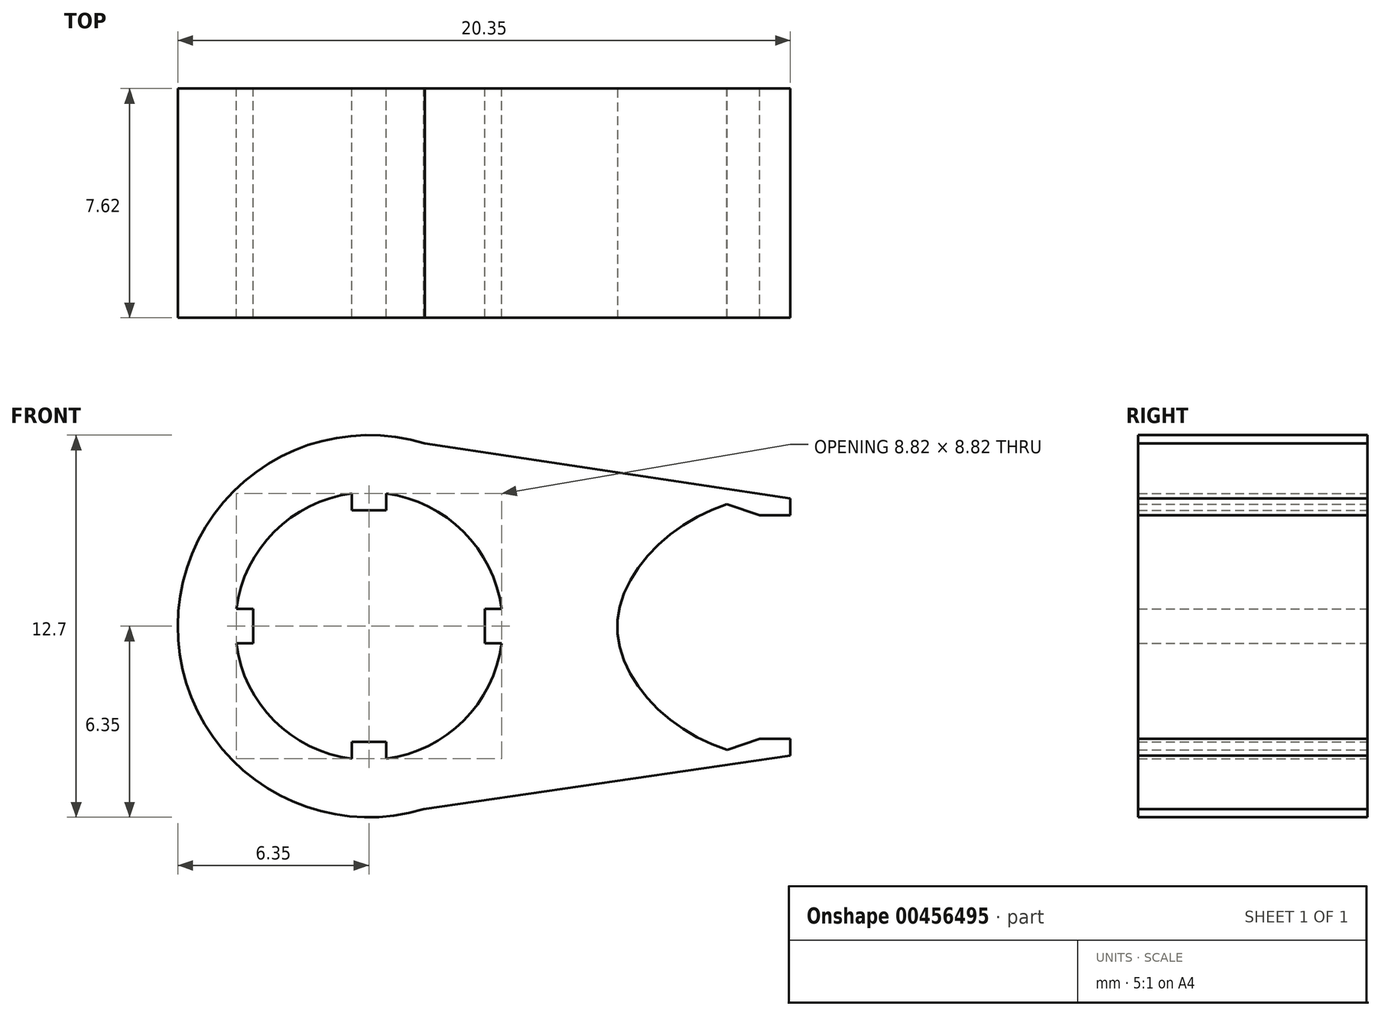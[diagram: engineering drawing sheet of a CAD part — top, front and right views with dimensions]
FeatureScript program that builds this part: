
annotation { "Feature Type Name" : "Feature", "Feature Type Description" : "" }
export const myFeature = defineFeature(function(context is Context, id is Id, definition is map)
    precondition{}
    {
        {
            var Q0;
            Q0=qCreatedBy(makeId("Front.planeOp"),FACE);
            var sketch = newSketch(context, id + "F0", { "sketchPlane" : qUnion([Q0])});
            skCircle(sketch, "E0", {"center": v(0, 0) * mm, "radius": 4.45 * mm});
            skCircle(sketch, "E1", {"center": v(0, 0) * mm, "radius": 6.35 * mm});
            skLineSegment(sketch, "E2", {"start": v(0, 6.35) * mm, "end": v(14, 4.25) * mm});
            skLineSegment(sketch, "E3", {"start": v(0, -6.35) * mm, "end": v(14, -4.3) * mm});
            skFitSpline(sketch, "E4", {"points": [v(14, 4.25) * mm, v(8.26, 0) * mm, v(14, -4.3) * mm], "startDerivative": vector(-15.84, 2.37) * mm, "endDerivative": vector(16.21, 2.37) * mm});
            skLineSegment(sketch, "E5", {"start": v(-0.57, 4.4) * mm, "end": v(-0.57, 3.85) * mm});
            skLineSegment(sketch, "E6", {"start": v(-0.57, 3.85) * mm, "end": v(0.57, 3.85) * mm});
            skLineSegment(sketch, "E7", {"start": v(0.57, 3.85) * mm, "end": v(0.57, 4.4) * mm});
            skLineSegment(sketch, "E8", {"start": v(-0.57, -4.4) * mm, "end": v(-0.57, -3.85) * mm});
            skLineSegment(sketch, "E9", {"start": v(-0.57, -3.85) * mm, "end": v(0.57, -3.85) * mm});
            skLineSegment(sketch, "E10", {"start": v(0.57, -3.85) * mm, "end": v(0.57, -4.4) * mm});
            skLineSegment(sketch, "E11", {"start": v(4.4, 0.57) * mm, "end": v(3.85, 0.57) * mm});
            skLineSegment(sketch, "E12", {"start": v(3.85, 0.57) * mm, "end": v(3.85, -0.57) * mm});
            skLineSegment(sketch, "E13", {"start": v(3.85, -0.57) * mm, "end": v(4.4, -0.57) * mm});
            skLineSegment(sketch, "E14", {"start": v(-4.4, 0.57) * mm, "end": v(-3.85, 0.57) * mm});
            skLineSegment(sketch, "E15", {"start": v(-3.85, 0.57) * mm, "end": v(-3.85, -0.57) * mm});
            skLineSegment(sketch, "E16", {"start": v(-3.85, -0.57) * mm, "end": v(-4.4, -0.57) * mm});
            skLineSegment(sketch, "E17", {"start": v(14, 4.25) * mm, "end": v(14, 3.7) * mm});
            skLineSegment(sketch, "E18", {"start": v(14, 3.7) * mm, "end": v(12.98, 3.7) * mm});
            skLineSegment(sketch, "E19", {"start": v(14, -4.3) * mm, "end": v(14, -3.74) * mm});
            skLineSegment(sketch, "E20", {"start": v(14, -3.74) * mm, "end": v(12.98, -3.74) * mm});
            skLineSegment(sketch, "E21", {"start": v(12.98, -4.33) * mm, "end": v(12.85, -4.28) * mm});
            skLineSegment(sketch, "E22", {"start": v(12.98, 3.7) * mm, "end": v(11.9, 4.05) * mm});
            skLineSegment(sketch, "E23", {"start": v(11.9, 4.05) * mm, "end": v(11.92, 3.98) * mm});
            skLineSegment(sketch, "E24", {"start": v(12.98, -3.74) * mm, "end": v(11.9, -4.1) * mm});
            skSolve(sketch);
        }
        {
            var Q0;
            Q0 = qSketchRegion(id + "F0", true);
            var Q1;
            {var subQ0=sQuery(id+"F0.wireOp",EDGE,"E11");Q1=makeQuery(id+"F0.imprint","IMPRINT",FACE,{"disambiguationData":[TD([[makeQuery(id+"F0.imprint","IMPRINT",EDGE,{"derivedFrom":subQ0}),1.0]])]});}
            var Q2;
            {var subQ0=sQuery(id+"F0.wireOp",EDGE,"E8");Q2=makeQuery(id+"F0.imprint","IMPRINT",FACE,{"disambiguationData":[TD([[makeQuery(id+"F0.imprint","IMPRINT",EDGE,{"derivedFrom":subQ0}),-1.0]])]});}
            var Q3;
            {var subQ0=sQuery(id+"F0.wireOp",EDGE,"E14");Q3=makeQuery(id+"F0.imprint","IMPRINT",FACE,{"disambiguationData":[TD([[makeQuery(id+"F0.imprint","IMPRINT",EDGE,{"derivedFrom":subQ0}),-1.0]])]});}
            var Q4;
            {var subQ0=sQuery(id+"F0.wireOp",EDGE,"E5");Q4=makeQuery(id+"F0.imprint","IMPRINT",FACE,{"disambiguationData":[TD([[makeQuery(id+"F0.imprint","IMPRINT",EDGE,{"derivedFrom":subQ0}),1.0]])]});}
            extrude(context, id + "F1", {"entities" : qUnion([Q0, Q1, Q2, Q3, Q4]), "depth" : 7.62 * mm, "offsetDistance" : 25.4 * mm});
        }
    });
